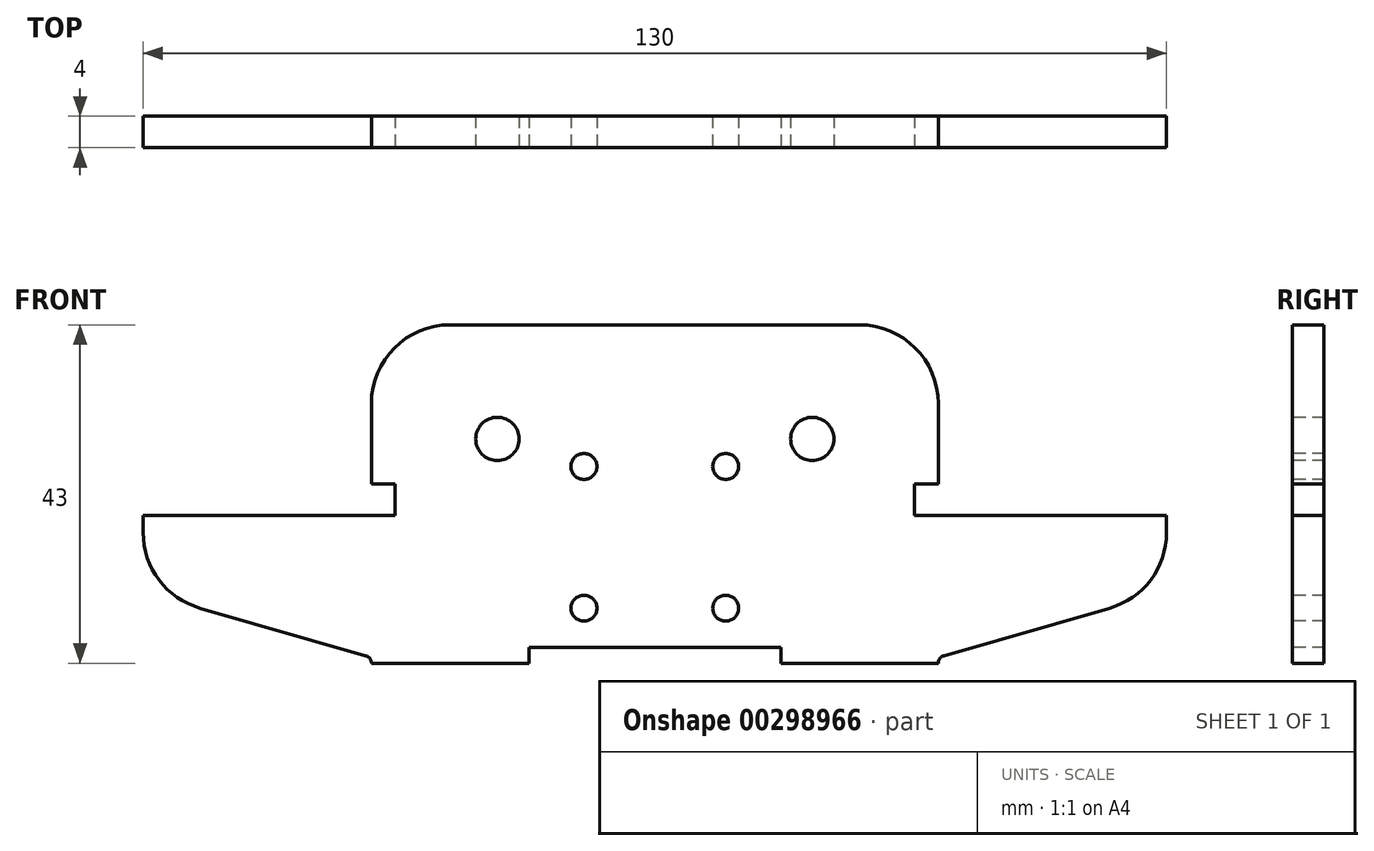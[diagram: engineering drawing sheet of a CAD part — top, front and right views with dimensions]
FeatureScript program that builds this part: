
annotation { "Feature Type Name" : "Feature", "Feature Type Description" : "" }
export const myFeature = defineFeature(function(context is Context, id is Id, definition is map)
    precondition{}
    {
        {
            var Q0;
            Q0=qCreatedBy(makeId("Front.planeOp"),FACE);
            var sketch = newSketch(context, id + "F0", { "sketchPlane" : qUnion([Q0])});
            skLineSegment(sketch, "E0", {"start": v(-36.17, 15.25) * mm, "end": v(-36.17, 5.05) * mm});
            skLineSegment(sketch, "E1", {"start": v(-33.17, 5.05) * mm, "end": v(-33.17, 1.05) * mm});
            skLineSegment(sketch, "E2", {"start": v(-36.9, -16.79) * mm, "end": v(-57.93, -10.76) * mm});
            skLineSegment(sketch, "E3", {"start": v(35.83, -17.75) * mm, "end": v(15.83, -17.75) * mm});
            skLineSegment(sketch, "E4", {"start": v(-16.17, -17.75) * mm, "end": v(-36.17, -17.75) * mm});
            skLineSegment(sketch, "E5", {"start": v(15.83, -15.75) * mm, "end": v(-16.17, -15.75) * mm});
            skLineSegment(sketch, "E6", {"start": v(57.58, -10.76) * mm, "end": v(36.55, -16.79) * mm});
            skLineSegment(sketch, "E7", {"start": v(-33.17, 1.05) * mm, "end": v(-65.17, 1.05) * mm});
            skLineSegment(sketch, "E8", {"start": v(32.83, 1.05) * mm, "end": v(64.83, 1.05) * mm});
            skLineSegment(sketch, "E9", {"start": v(32.83, 1.05) * mm, "end": v(32.83, 5.05) * mm});
            skLineSegment(sketch, "E10", {"start": v(35.83, 15.25) * mm, "end": v(35.83, 5.05) * mm});
            skLineSegment(sketch, "E11", {"start": v(-26.17, 25.25) * mm, "end": v(25.83, 25.25) * mm});
            skArc(sketch, "E12", {"start": v(-36.17, -17.75) * mm, "mid": v(-36.38, -17.15) * mm, "end": v(-36.9, -16.79) * mm});
            skArc(sketch, "E13", {"start": v(-26.17, 25.25) * mm, "mid": v(-33.24, 22.32) * mm, "end": v(-36.17, 15.25) * mm});
            skArc(sketch, "E14", {"start": v(-65.17, -1.14) * mm, "mid": v(-63.16, -7.16) * mm, "end": v(-57.93, -10.76) * mm});
            skCircle(sketch, "E15", {"center": v(-20.17, 10.75) * mm, "radius": 2.75 * mm});
            skCircle(sketch, "E16", {"center": v(-9.17, -10.75) * mm, "radius": 1.65 * mm});
            skCircle(sketch, "E17", {"center": v(-9.17, 7.25) * mm, "radius": 1.65 * mm});
            skArc(sketch, "E18", {"start": v(36.55, -16.79) * mm, "mid": v(36.03, -17.15) * mm, "end": v(35.83, -17.75) * mm});
            skArc(sketch, "E19", {"start": v(57.58, -10.76) * mm, "mid": v(62.81, -7.16) * mm, "end": v(64.83, -1.14) * mm});
            skArc(sketch, "E20", {"start": v(35.83, 15.25) * mm, "mid": v(32.9, 22.32) * mm, "end": v(25.83, 25.25) * mm});
            skCircle(sketch, "E21", {"center": v(19.83, 10.75) * mm, "radius": 2.75 * mm});
            skCircle(sketch, "E22", {"center": v(8.83, -10.75) * mm, "radius": 1.65 * mm});
            skCircle(sketch, "E23", {"center": v(8.83, 7.25) * mm, "radius": 1.65 * mm});
            skLineSegment(sketch, "E24", {"start": v(35.83, 5.05) * mm, "end": v(32.83, 5.05) * mm});
            skLineSegment(sketch, "E25", {"start": v(-36.17, 5.05) * mm, "end": v(-33.17, 5.05) * mm});
            skLineSegment(sketch, "E26", {"start": v(-65.17, -1.14) * mm, "end": v(-65.17, 1.05) * mm});
            skLineSegment(sketch, "E27", {"start": v(64.83, -1.14) * mm, "end": v(64.83, 1.05) * mm});
            skLineSegment(sketch, "E28", {"start": v(15.83, -17.75) * mm, "end": v(15.83, -15.75) * mm});
            skLineSegment(sketch, "E29", {"start": v(-16.17, -17.75) * mm, "end": v(-16.17, -15.75) * mm});
            skSolve(sketch);
        }
        {
            var Q0;
            Q0 = qConstructionFilter(qBodyType(qCreatedBy(id + "F0" ,EDGE), BodyType.WIRE), ConstructionObject.NO);
            extrude(context, id + "F1", {"bodyType" : ToolBodyType.SURFACE, "surfaceEntities" : qUnion([Q0]), "depth" : 4 * mm});
        }
    });
